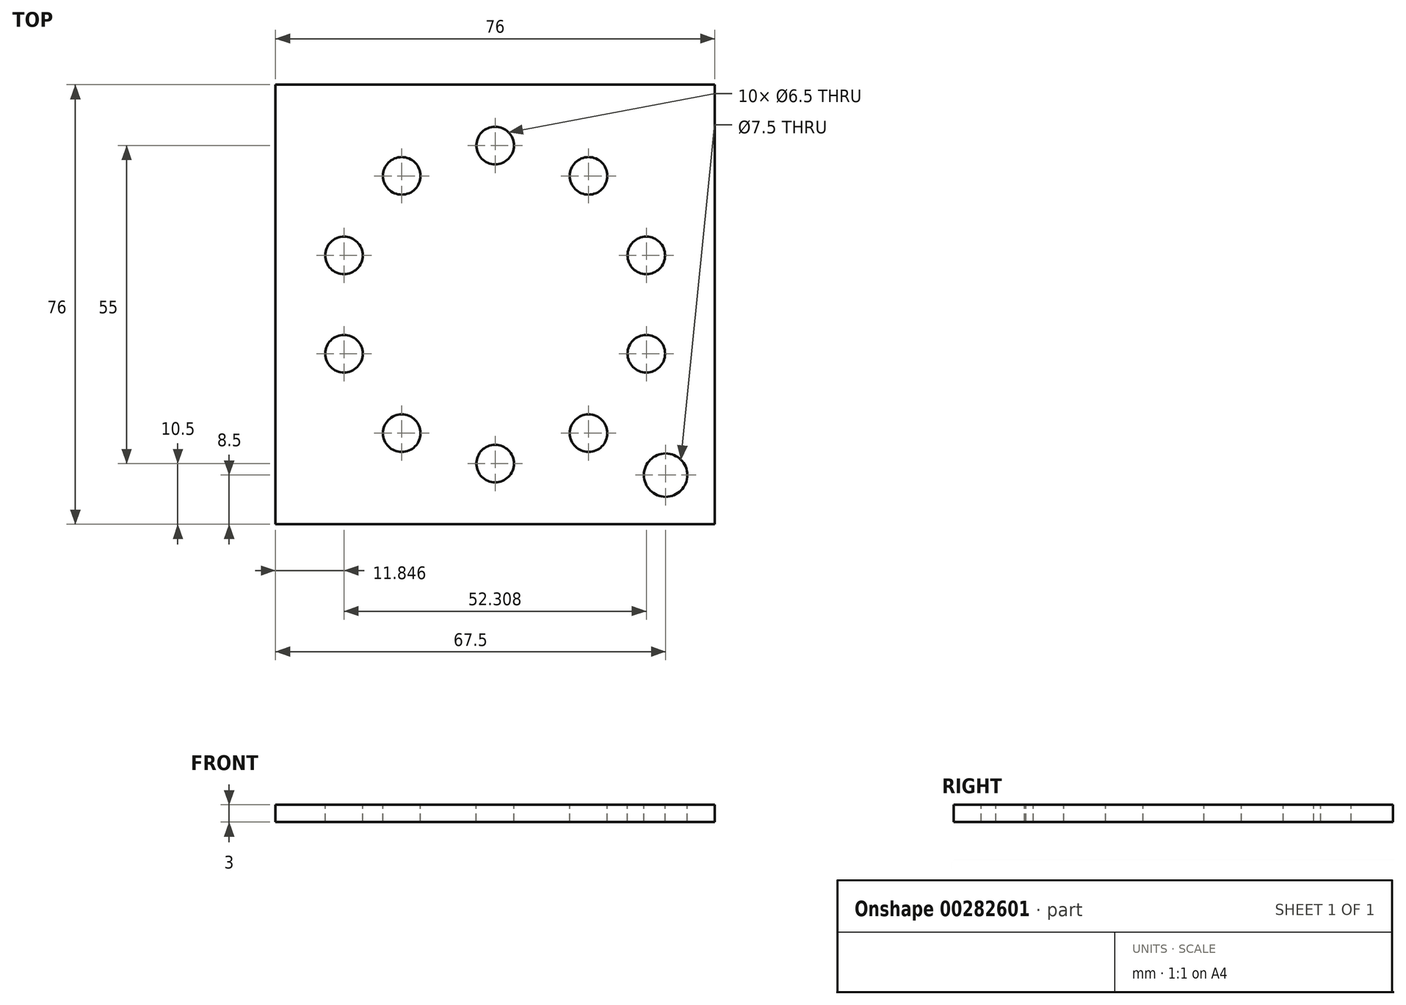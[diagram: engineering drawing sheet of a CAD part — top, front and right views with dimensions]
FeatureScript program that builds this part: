
annotation { "Feature Type Name" : "Feature", "Feature Type Description" : "" }
export const myFeature = defineFeature(function(context is Context, id is Id, definition is map)
    precondition{}
    {
        {
            var Q0;
            Q0=qCreatedBy(makeId("Top.planeOp"),FACE);
            var sketch = newSketch(context, id + "F0", { "sketchPlane" : qUnion([Q0])});
            skLineSegment(sketch, "E0.bottom", {"start": v(-38, 38) * mm, "end": v(38, 38) * mm});
            skLineSegment(sketch, "E0.top", {"start": v(-38, -38) * mm, "end": v(38, -38) * mm});
            skLineSegment(sketch, "E0.left", {"start": v(-38, 38) * mm, "end": v(-38, -38) * mm});
            skLineSegment(sketch, "E0.right", {"start": v(38, 38) * mm, "end": v(38, -38) * mm});
            skPoint(sketch, "E0.middle", {"position": v(0, 0) * mm});
            skSolve(sketch);
        }
        {
            var Q0;
            Q0 = qSketchRegion(id + "F0", true);
            extrude(context, id + "F1", {"entities" : qUnion([Q0]), "depth" : 3 * mm});
        }
        {
            var Q0;
            Q0=makeQuery(id+"F1.opExtrude","CAP_FACE",FACE,{"disambiguationData":[OSD([sQuery(id+"F0.wireOp",EDGE,"E0.bottom"),sQuery(id+"F0.wireOp",EDGE,"E0.top"),sQuery(id+"F0.wireOp",EDGE,"E0.left"),sQuery(id+"F0.wireOp",EDGE,"E0.right")])],"isStart":false});
            var sketch = newSketch(context, id + "F2", { "sketchPlane" : qUnion([Q0])});
            skCircle(sketch, "E1", {"center": v(0, 0) * mm, "radius": 35 * mm});
            skCircle(sketch, "E2", {"center": v(0, 0) * mm, "radius": 27.5 * mm});
            skCircle(sketch, "E3", {"center": v(0, 27.5) * mm, "radius": 3.25 * mm});
            skCircle(sketch, "E4.1.0", {"center": v(-16.16, 22.25) * mm, "radius": 3.25 * mm});
            skCircle(sketch, "E4.2.0", {"center": v(-26.15, 8.5) * mm, "radius": 3.25 * mm});
            skCircle(sketch, "E4.3.0", {"center": v(-26.15, -8.5) * mm, "radius": 3.25 * mm});
            skCircle(sketch, "E4.4.0", {"center": v(-16.16, -22.25) * mm, "radius": 3.25 * mm});
            skCircle(sketch, "E4.5.0", {"center": v(0, -27.5) * mm, "radius": 3.25 * mm});
            skCircle(sketch, "E4.6.0", {"center": v(16.16, -22.25) * mm, "radius": 3.25 * mm});
            skCircle(sketch, "E4.7.0", {"center": v(26.15, -8.5) * mm, "radius": 3.25 * mm});
            skCircle(sketch, "E4.8.0", {"center": v(26.15, 8.5) * mm, "radius": 3.25 * mm});
            skCircle(sketch, "E4.9.0", {"center": v(16.16, 22.25) * mm, "radius": 3.25 * mm});
            skSolve(sketch);
        }
        {
            var Q0;
            {var subQ0=sQuery(id+"F2.wireOp",EDGE,"E3");var subQ1=sQuery(id+"F2.wireOp",EDGE,"E2");var subQ2=makeQuery(id+"F2.imprint","INTERSECT",VERTEX,{"disambiguationData":[OD(0.0)],"derivedFrom":[subQ1,subQ0]});Q0=makeQuery(id+"F2.imprint","IMPRINT",FACE,{"disambiguationData":[TD([[makeQuery(id+"F2.imprint","IMPRINT",EDGE,{"disambiguationData":[TD([[subQ2,-1.0]])],"derivedFrom":subQ1}),-1.0]])]});}
            var Q1;
            {var subQ0=sQuery(id+"F2.wireOp",EDGE,"E3");var subQ1=sQuery(id+"F2.wireOp",EDGE,"E2");var subQ2=makeQuery(id+"F2.imprint","INTERSECT",VERTEX,{"disambiguationData":[OD(0.0)],"derivedFrom":[subQ1,subQ0]});Q1=makeQuery(id+"F2.imprint","IMPRINT",FACE,{"disambiguationData":[TD([[makeQuery(id+"F2.imprint","IMPRINT",EDGE,{"disambiguationData":[TD([[subQ2,-1.0]])],"derivedFrom":subQ1}),1.0]])]});}
            var Q2;
            {var subQ0=sQuery(id+"F2.wireOp",EDGE,"E4.9.0");var subQ1=sQuery(id+"F2.wireOp",EDGE,"E2");var subQ2=makeQuery(id+"F2.imprint","INTERSECT",VERTEX,{"disambiguationData":[OD(0.0)],"derivedFrom":[subQ1,subQ0]});Q2=makeQuery(id+"F2.imprint","IMPRINT",FACE,{"disambiguationData":[TD([[makeQuery(id+"F2.imprint","IMPRINT",EDGE,{"disambiguationData":[TD([[subQ2,-1.0]])],"derivedFrom":subQ1}),-1.0]])]});}
            var Q3;
            {var subQ0=sQuery(id+"F2.wireOp",EDGE,"E4.9.0");var subQ1=sQuery(id+"F2.wireOp",EDGE,"E2");var subQ2=makeQuery(id+"F2.imprint","INTERSECT",VERTEX,{"disambiguationData":[OD(0.0)],"derivedFrom":[subQ1,subQ0]});Q3=makeQuery(id+"F2.imprint","IMPRINT",FACE,{"disambiguationData":[TD([[makeQuery(id+"F2.imprint","IMPRINT",EDGE,{"disambiguationData":[TD([[subQ2,-1.0]])],"derivedFrom":subQ1}),1.0]])]});}
            var Q4;
            {var subQ0=sQuery(id+"F2.wireOp",EDGE,"E4.8.0");var subQ1=sQuery(id+"F2.wireOp",EDGE,"E2");var subQ2=makeQuery(id+"F2.imprint","INTERSECT",VERTEX,{"disambiguationData":[OD(0.0)],"derivedFrom":[subQ1,subQ0]});Q4=makeQuery(id+"F2.imprint","IMPRINT",FACE,{"disambiguationData":[TD([[makeQuery(id+"F2.imprint","IMPRINT",EDGE,{"disambiguationData":[TD([[subQ2,1.0]])],"derivedFrom":subQ1}),-1.0]])]});}
            var Q5;
            {var subQ0=sQuery(id+"F2.wireOp",EDGE,"E4.8.0");var subQ1=sQuery(id+"F2.wireOp",EDGE,"E2");var subQ2=makeQuery(id+"F2.imprint","INTERSECT",VERTEX,{"disambiguationData":[OD(0.0)],"derivedFrom":[subQ1,subQ0]});Q5=makeQuery(id+"F2.imprint","IMPRINT",FACE,{"disambiguationData":[TD([[makeQuery(id+"F2.imprint","IMPRINT",EDGE,{"disambiguationData":[TD([[subQ2,1.0]])],"derivedFrom":subQ1}),1.0]])]});}
            var Q6;
            {var subQ0=sQuery(id+"F2.wireOp",EDGE,"E4.7.0");var subQ1=sQuery(id+"F2.wireOp",EDGE,"E2");var subQ2=makeQuery(id+"F2.imprint","INTERSECT",VERTEX,{"disambiguationData":[OD(0.0)],"derivedFrom":[subQ1,subQ0]});Q6=makeQuery(id+"F2.imprint","IMPRINT",FACE,{"disambiguationData":[TD([[makeQuery(id+"F2.imprint","IMPRINT",EDGE,{"disambiguationData":[TD([[subQ2,-1.0]])],"derivedFrom":subQ1}),-1.0]])]});}
            var Q7;
            {var subQ0=sQuery(id+"F2.wireOp",EDGE,"E4.7.0");var subQ1=sQuery(id+"F2.wireOp",EDGE,"E2");var subQ2=makeQuery(id+"F2.imprint","INTERSECT",VERTEX,{"disambiguationData":[OD(0.0)],"derivedFrom":[subQ1,subQ0]});Q7=makeQuery(id+"F2.imprint","IMPRINT",FACE,{"disambiguationData":[TD([[makeQuery(id+"F2.imprint","IMPRINT",EDGE,{"disambiguationData":[TD([[subQ2,-1.0]])],"derivedFrom":subQ1}),1.0]])]});}
            var Q8;
            {var subQ0=sQuery(id+"F2.wireOp",EDGE,"E4.6.0");var subQ1=sQuery(id+"F2.wireOp",EDGE,"E2");var subQ2=makeQuery(id+"F2.imprint","INTERSECT",VERTEX,{"disambiguationData":[OD(0.0)],"derivedFrom":[subQ1,subQ0]});Q8=makeQuery(id+"F2.imprint","IMPRINT",FACE,{"disambiguationData":[TD([[makeQuery(id+"F2.imprint","IMPRINT",EDGE,{"disambiguationData":[TD([[subQ2,-1.0]])],"derivedFrom":subQ1}),1.0]])]});}
            var Q9;
            {var subQ0=sQuery(id+"F2.wireOp",EDGE,"E4.6.0");var subQ1=sQuery(id+"F2.wireOp",EDGE,"E2");var subQ2=makeQuery(id+"F2.imprint","INTERSECT",VERTEX,{"disambiguationData":[OD(0.0)],"derivedFrom":[subQ1,subQ0]});Q9=makeQuery(id+"F2.imprint","IMPRINT",FACE,{"disambiguationData":[TD([[makeQuery(id+"F2.imprint","IMPRINT",EDGE,{"disambiguationData":[TD([[subQ2,-1.0]])],"derivedFrom":subQ1}),-1.0]])]});}
            var Q10;
            {var subQ0=sQuery(id+"F2.wireOp",EDGE,"E4.5.0");var subQ1=sQuery(id+"F2.wireOp",EDGE,"E2");var subQ2=makeQuery(id+"F2.imprint","INTERSECT",VERTEX,{"disambiguationData":[OD(0.0)],"derivedFrom":[subQ1,subQ0]});Q10=makeQuery(id+"F2.imprint","IMPRINT",FACE,{"disambiguationData":[TD([[makeQuery(id+"F2.imprint","IMPRINT",EDGE,{"disambiguationData":[TD([[subQ2,-1.0]])],"derivedFrom":subQ1}),1.0]])]});}
            var Q11;
            {var subQ0=sQuery(id+"F2.wireOp",EDGE,"E4.5.0");var subQ1=sQuery(id+"F2.wireOp",EDGE,"E2");var subQ2=makeQuery(id+"F2.imprint","INTERSECT",VERTEX,{"disambiguationData":[OD(0.0)],"derivedFrom":[subQ1,subQ0]});Q11=makeQuery(id+"F2.imprint","IMPRINT",FACE,{"disambiguationData":[TD([[makeQuery(id+"F2.imprint","IMPRINT",EDGE,{"disambiguationData":[TD([[subQ2,-1.0]])],"derivedFrom":subQ1}),-1.0]])]});}
            var Q12;
            {var subQ0=sQuery(id+"F2.wireOp",EDGE,"E4.4.0");var subQ1=sQuery(id+"F2.wireOp",EDGE,"E2");var subQ2=makeQuery(id+"F2.imprint","INTERSECT",VERTEX,{"disambiguationData":[OD(0.0)],"derivedFrom":[subQ1,subQ0]});Q12=makeQuery(id+"F2.imprint","IMPRINT",FACE,{"disambiguationData":[TD([[makeQuery(id+"F2.imprint","IMPRINT",EDGE,{"disambiguationData":[TD([[subQ2,-1.0]])],"derivedFrom":subQ1}),-1.0]])]});}
            var Q13;
            {var subQ0=sQuery(id+"F2.wireOp",EDGE,"E4.4.0");var subQ1=sQuery(id+"F2.wireOp",EDGE,"E2");var subQ2=makeQuery(id+"F2.imprint","INTERSECT",VERTEX,{"disambiguationData":[OD(0.0)],"derivedFrom":[subQ1,subQ0]});Q13=makeQuery(id+"F2.imprint","IMPRINT",FACE,{"disambiguationData":[TD([[makeQuery(id+"F2.imprint","IMPRINT",EDGE,{"disambiguationData":[TD([[subQ2,-1.0]])],"derivedFrom":subQ1}),1.0]])]});}
            var Q14;
            {var subQ0=sQuery(id+"F2.wireOp",EDGE,"E4.3.0");var subQ1=sQuery(id+"F2.wireOp",EDGE,"E2");var subQ2=makeQuery(id+"F2.imprint","INTERSECT",VERTEX,{"disambiguationData":[OD(0.0)],"derivedFrom":[subQ1,subQ0]});Q14=makeQuery(id+"F2.imprint","IMPRINT",FACE,{"disambiguationData":[TD([[makeQuery(id+"F2.imprint","IMPRINT",EDGE,{"disambiguationData":[TD([[subQ2,-1.0]])],"derivedFrom":subQ1}),-1.0]])]});}
            var Q15;
            {var subQ0=sQuery(id+"F2.wireOp",EDGE,"E4.3.0");var subQ1=sQuery(id+"F2.wireOp",EDGE,"E2");var subQ2=makeQuery(id+"F2.imprint","INTERSECT",VERTEX,{"disambiguationData":[OD(0.0)],"derivedFrom":[subQ1,subQ0]});Q15=makeQuery(id+"F2.imprint","IMPRINT",FACE,{"disambiguationData":[TD([[makeQuery(id+"F2.imprint","IMPRINT",EDGE,{"disambiguationData":[TD([[subQ2,-1.0]])],"derivedFrom":subQ1}),1.0]])]});}
            var Q16;
            {var subQ0=sQuery(id+"F2.wireOp",EDGE,"E4.2.0");var subQ1=sQuery(id+"F2.wireOp",EDGE,"E2");var subQ2=makeQuery(id+"F2.imprint","INTERSECT",VERTEX,{"disambiguationData":[OD(0.0)],"derivedFrom":[subQ1,subQ0]});Q16=makeQuery(id+"F2.imprint","IMPRINT",FACE,{"disambiguationData":[TD([[makeQuery(id+"F2.imprint","IMPRINT",EDGE,{"disambiguationData":[TD([[subQ2,-1.0]])],"derivedFrom":subQ1}),1.0]])]});}
            var Q17;
            {var subQ0=sQuery(id+"F2.wireOp",EDGE,"E4.2.0");var subQ1=sQuery(id+"F2.wireOp",EDGE,"E2");var subQ2=makeQuery(id+"F2.imprint","INTERSECT",VERTEX,{"disambiguationData":[OD(0.0)],"derivedFrom":[subQ1,subQ0]});Q17=makeQuery(id+"F2.imprint","IMPRINT",FACE,{"disambiguationData":[TD([[makeQuery(id+"F2.imprint","IMPRINT",EDGE,{"disambiguationData":[TD([[subQ2,-1.0]])],"derivedFrom":subQ1}),-1.0]])]});}
            var Q18;
            {var subQ0=sQuery(id+"F2.wireOp",EDGE,"E4.1.0");var subQ1=sQuery(id+"F2.wireOp",EDGE,"E2");var subQ2=makeQuery(id+"F2.imprint","INTERSECT",VERTEX,{"disambiguationData":[OD(0.0)],"derivedFrom":[subQ1,subQ0]});Q18=makeQuery(id+"F2.imprint","IMPRINT",FACE,{"disambiguationData":[TD([[makeQuery(id+"F2.imprint","IMPRINT",EDGE,{"disambiguationData":[TD([[subQ2,-1.0]])],"derivedFrom":subQ1}),1.0]])]});}
            var Q19;
            {var subQ0=sQuery(id+"F2.wireOp",EDGE,"E4.1.0");var subQ1=sQuery(id+"F2.wireOp",EDGE,"E2");var subQ2=makeQuery(id+"F2.imprint","INTERSECT",VERTEX,{"disambiguationData":[OD(0.0)],"derivedFrom":[subQ1,subQ0]});Q19=makeQuery(id+"F2.imprint","IMPRINT",FACE,{"disambiguationData":[TD([[makeQuery(id+"F2.imprint","IMPRINT",EDGE,{"disambiguationData":[TD([[subQ2,-1.0]])],"derivedFrom":subQ1}),-1.0]])]});}
            extrude(context, id + "F3", {"entities" : qUnion([Q0, Q1, Q2, Q3, Q4, Q5, Q6, Q7, Q8, Q9, Q10, Q11, Q12, Q13, Q14, Q15, Q16, Q17, Q18, Q19]), "operationType" : NewBodyOperationType.REMOVE, "oppositeDirection" : true, "depth" : 25 * mm});
        }
        {
            var Q0;
            Q0=makeQuery(id+"F1.opExtrude","CAP_FACE",FACE,{"disambiguationData":[OSD([sQuery(id+"F0.wireOp",EDGE,"E0.bottom"),sQuery(id+"F0.wireOp",EDGE,"E0.top"),sQuery(id+"F0.wireOp",EDGE,"E0.left"),sQuery(id+"F0.wireOp",EDGE,"E0.right")])],"isStart":false});
            var sketch = newSketch(context, id + "F4", { "sketchPlane" : qUnion([Q0])});
            skCircle(sketch, "E5", {"center": v(29.5, -29.5) * mm, "radius": 3.75 * mm});
            skSolve(sketch);
        }
        {
            var Q0;
            Q0=makeQuery(id+"F4.imprint","IMPRINT",FACE,{"disambiguationData":[TD([[makeQuery(id+"F4.imprint","IMPRINT",EDGE,{"derivedFrom":sQuery(id+"F4.wireOp",EDGE,"E5")}),1.0]])]});
            extrude(context, id + "F5", {"entities" : qUnion([Q0]), "operationType" : NewBodyOperationType.REMOVE, "oppositeDirection" : true, "depth" : 25 * mm});
        }
    });
